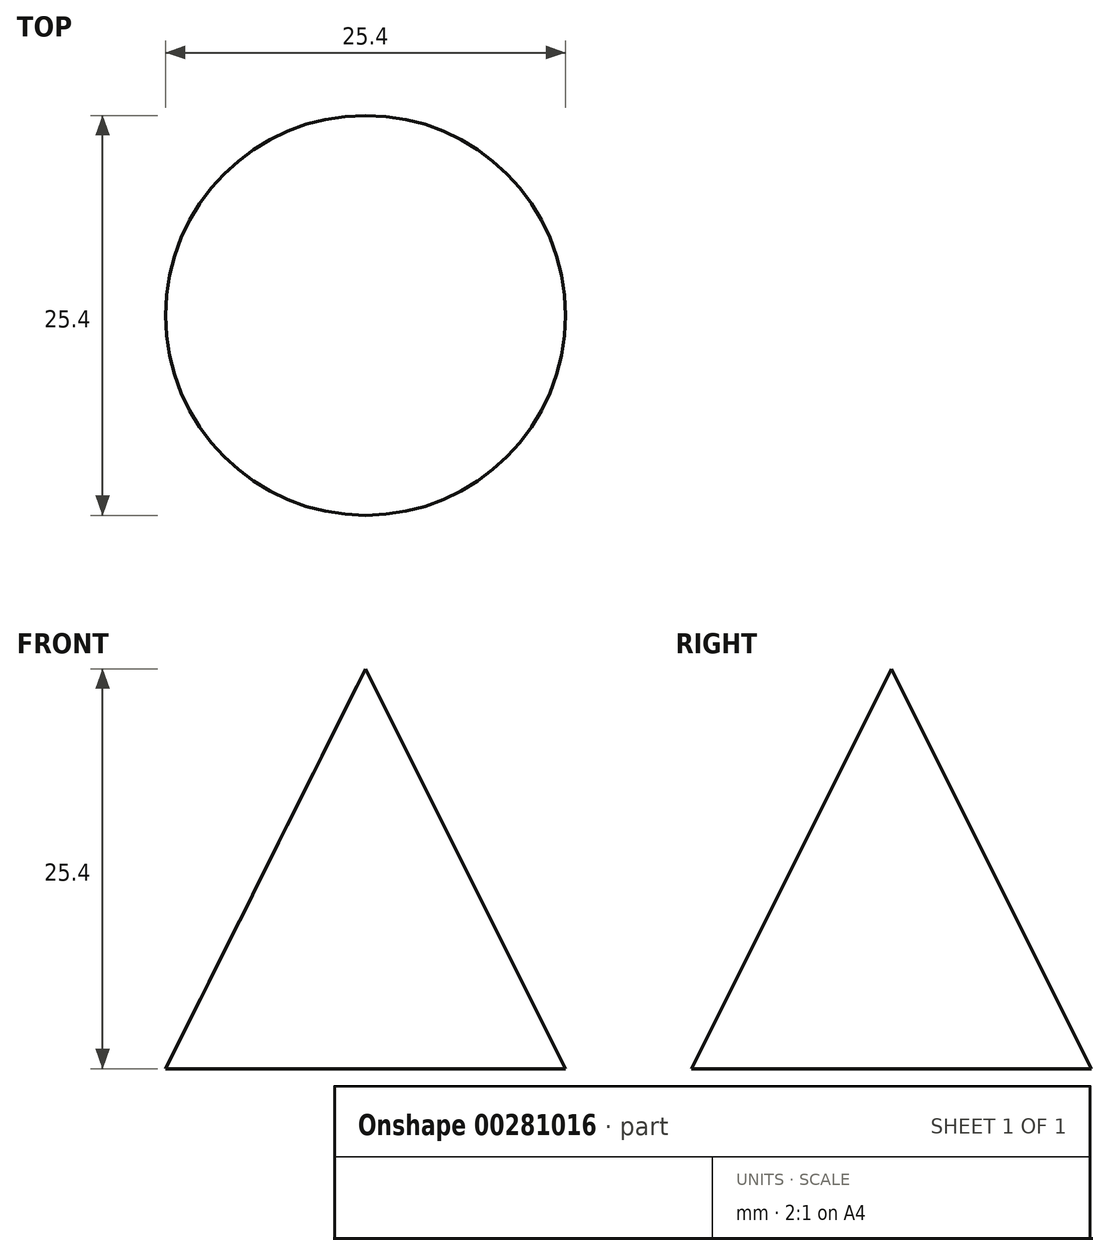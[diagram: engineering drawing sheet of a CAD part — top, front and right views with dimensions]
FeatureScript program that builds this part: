
annotation { "Feature Type Name" : "Feature", "Feature Type Description" : "" }
export const myFeature = defineFeature(function(context is Context, id is Id, definition is map)
    precondition{}
    {
        {
            var Q0;
            Q0=qCreatedBy(makeId("Top.planeOp"),FACE);
            var sketch = newSketch(context, id + "F0", { "sketchPlane" : qUnion([Q0])});
            skCircle(sketch, "E0", {"center": v(0, 0) * mm, "radius": 12.7 * mm});
            skSolve(sketch);
        }
        {
            var Q0;
            Q0=qCreatedBy(makeId("Top.planeOp"),FACE);
            cPlane(context, id + "F1", {"entities" : qUnion([Q0]), "cplaneType" : CPlaneType.OFFSET, "offset" : 25.4 * mm, "width" : 152.4 * mm, "height" : 152.4 * mm});
        }
        {
            var Q0;
            Q0=qCreatedBy(id+"F1.planeOp",FACE);
            var sketch = newSketch(context, id + "F2", { "sketchPlane" : qUnion([Q0])});
            skPoint(sketch, "E1", {"position": v(0, 0) * mm});
            skSolve(sketch);
        }
        {
            var Q0;
            Q0=makeQuery(id+"F0.imprint","IMPRINT",FACE,{"disambiguationData":[TD([[makeQuery(id+"F0.imprint","IMPRINT",EDGE,{"derivedFrom":sQuery(id+"F0.wireOp",EDGE,"E0")}),1.0]])]});
            var Q1;
            Q1=sQuery(id+"F2.wireOp",VERTEX,"E1");
            loft(context, id + "F3", {"sheetProfilesArray" : [{ "sheetProfileEntities" : qUnion([Q0]) }, { "sheetProfileEntities" : qUnion([Q1]) }]});
        }
    });
